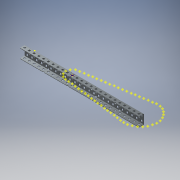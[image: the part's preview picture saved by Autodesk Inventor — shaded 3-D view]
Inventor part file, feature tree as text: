
AUTODESK INVENTOR PART (.ipt)
format: ipt  version: 2018 (Build 220112000, 112)  size: 2,780,672 bytes
history: native  units: mm (DEFAULTED — no unit token found)
features: other x277, extrude x124, sketch x4, pattern_linear x4, reference x2, imported_body x1, plane x1, mirror x1
ambient origin geometry x8: Origin, YZ Plane, XZ Plane, XY Plane, X Axis, Y Axis, Z Axis, Center Point
bodies: Solid1 (feature_tree)
feature tree (414):
  imported_body  "Base1"
  sketch  "Sketch1"  dims[d1=1.1684mm]
  pattern_linear  "Rectangular Pattern1"  Count1=25  [1 undecoded]
  pattern_linear  "Rectangular Pattern2"  Spacing1=12.7mm  [1 undecoded]
  pattern_linear  "Rectangular Pattern3"  Count1=2 Spacing1=12.7mm
  plane  "Work Plane1"
  mirror  "Mirror1"
  sketch  "Sketch3"  dims[d3=1.1684mm]
  sketch  "Sketch4"  dims[d4=0.0mm d5=250.0mm d7=12.7mm d8=20.0mm d10=12.7mm d11=240.0mm d13=12.7mm d14=1.1684mm d15=0.0mm d16=250.0mm d18=12.7mm d19=0.0mm d20=0.0mm d21=0.0mm d22=0.0mm d23=0.0mm d24=0.0mm d25=0.0mm d26=0.0mm d27=0.0mm d28=0.0mm d29=0.0mm d30=0.0mm d31=0.0mm d32=0.0mm d33=0.0mm d34=0.0mm d35=0.0mm d36=0.0mm d37=0.0mm d38=0.0mm d39=0.0mm d40=0.0mm d41=0.0mm d42=0.0mm d43=0.0mm d44=0.0mm d45=0.0mm d46=0.0mm d47=0.0mm d48=0.0mm d49=0.0mm d50=0.0mm d51=0.0mm d52=0.0mm d53=0.0mm d54=0.0mm d55=0.0mm d56=0.0mm d57=0.0mm d58=0.0mm d59=0.0mm d60=0.0mm d61=0.0mm d62=0.0mm d63=0.0mm d64=0.0mm d65=0.0mm d66=0.0mm d67=0.0mm d68=0.0mm d69=0.0mm d70=0.0mm d71=0.0mm d72=0.0mm d73=0.0mm d74=0.0mm d75=0.0mm d76=0.0mm d77=0.0mm d78=0.0mm d79=0.0mm d80=0.0mm d81=0.0mm d82=0.0mm d83=0.0mm d84=0.0mm d85=0.0mm d86=0.0mm d87=0.0mm d88=0.0mm d89=0.0mm d90=0.0mm d91=0.0mm d92=0.0mm d93=0.0mm d94=0.0mm d95=0.0mm d96=0.0mm d97=0.0mm d98=0.0mm d99=0.0mm d100=0.0mm d101=0.0mm d102=0.0mm d103=0.0mm d104=0.0mm d105=0.0mm d106=0.0mm d107=0.0mm d108=0.0mm d109=0.0mm d110=0.0mm d111=0.0mm d112=0.0mm d113=0.0mm d114=0.0mm d115=0.0mm d116=0.0mm d117=0.0mm d118=0.0mm d119=0.0mm d120=0.0mm d121=0.0mm d122=0.0mm d123=0.0mm d124=0.0mm d125=0.0mm d126=0.0mm d127=0.0mm d128=0.0mm d129=0.0mm d130=0.0mm d131=0.0mm d132=0.0mm d133=0.0mm d134=0.0mm d135=0.0mm d136=0.0mm d137=0.0mm d138=0.0mm d139=0.0mm d140=0.0mm d141=0.0mm d142=0.0mm d143=0.0mm d144=0.0mm d145=0.0mm d146=0.0mm d147=0.0mm d148=0.0mm d149=0.0mm d150=0.0mm d151=0.0mm d152=0.0mm d153=0.0mm d154=0.0mm d155=0.0mm d156=0.0mm d157=0.0mm d158=0.0mm d159=0.0mm d160=0.0mm d161=0.0mm d162=0.0mm d163=0.0mm d164=0.0mm d165=0.0mm d166=0.0mm d167=0.0mm d168=0.0mm d169=0.0mm d170=0.0mm d171=0.0mm d172=0.0mm d173=0.0mm d174=0.0mm d175=0.0mm d176=0.0mm d177=0.0mm d178=0.0mm d179=0.0mm d180=0.0mm d181=0.0mm d182=0.0mm d183=0.0mm d184=0.0mm d185=0.0mm d186=0.0mm d187=0.0mm d188=0.0mm d189=0.0mm d190=0.0mm d191=0.0mm d192=0.0mm d193=0.0mm d194=0.0mm d195=0.0mm d196=0.0mm d197=0.0mm d198=0.0mm d199=0.0mm d200=0.0mm d201=0.0mm d202=0.0mm d203=0.0mm d204=0.0mm d205=0.0mm d206=0.0mm d207=0.0mm d208=0.0mm d209=0.0mm d210=0.0mm d211=0.0mm d212=0.0mm d213=0.0mm d214=0.0mm d215=0.0mm d216=0.0mm d217=0.0mm d218=0.0mm d219=0.0mm d220=0.0mm d221=0.0mm d222=0.0mm d223=0.0mm d224=0.0mm d225=0.0mm d226=0.0mm d227=0.0mm d228=0.0mm d229=0.0mm d230=0.0mm d231=0.0mm d232=0.0mm d233=0.0mm d234=0.0mm d235=0.0mm d236=0.0mm d237=0.0mm d238=0.0mm d239=0.0mm d240=0.0mm d241=0.0mm d242=0.0mm d243=0.0mm d244=0.0mm d245=0.0mm d246=0.0mm d247=0.0mm d248=0.0mm d249=0.0mm d250=0.0mm d251=0.0mm d252=0.0mm d253=0.0mm d254=0.0mm d255=0.0mm d256=0.0mm d257=0.0mm d258=0.0mm d259=0.0mm d260=0.0mm d261=0.0mm d262=0.0mm d263=0.0mm d264=1500.0mm d266=3.715mm]
  other  "Work Point1"
  pattern_linear  "Rectangular Pattern4"  Count1=24  [1 undecoded]
  other  "Srf1"
  other  "Srf2"
  other  "Srf3"
  other  "Srf4"
  other  "Srf5"
  other  "Srf6"
  other  "Srf7"
  other  "Srf8"
  other  "Srf9"
  other  "Srf10"
  other  "Srf11"
  other  "Srf12"
  other  "Srf13"
  other  "Srf14"
  other  "Srf15"
  other  "Srf16"
  other  "Srf17"
  other  "Srf18"
  other  "Srf19"
  other  "Srf20"
  other  "Srf21"
  other  "Srf22"
  other  "Srf23"
  other  "Srf24"
  other  "Srf25"
  other  "Srf26"
  other  "Srf27"
  other  "Srf28"
  other  "Srf29"
  other  "Srf30"
  other  "Srf31"
  other  "Srf32"
  other  "Srf33"
  other  "Srf34"
  other  "Srf35"
  other  "Srf36"
  other  "Srf37"
  other  "Srf38"
  other  "Srf39"
  other  "Srf40"
  other  "Srf41"
  other  "Srf42"
  other  "Srf43"
  other  "Srf44"
  other  "Srf45"
  other  "Srf46"
  other  "Srf47"
  other  "Srf48"
  other  "Srf49"
  other  "Srf50"
  other  "Srf51"
  other  "Srf52"
  other  "Srf53"
  other  "Srf54"
  other  "Srf55"
  other  "Srf56"
  other  "Srf57"
  other  "Srf58"
  other  "Srf59"
  other  "Srf60"
  other  "Srf61"
  other  "Srf62"
  other  "Srf63"
  other  "Srf64"
  other  "Srf65"
  other  "Srf66"
  other  "Srf67"
  other  "Srf68"
  other  "Srf69"
  other  "Srf70"
  other  "Srf71"
  other  "Srf72"
  other  "Srf73"
  other  "Srf74"
  sketch  "Sketch2"  dims[d2=0.0mm]
  other  "Srf75"
  other  "Srf76"
  other  "Srf77"
  other  "Srf78"
  other  "Srf79"
  other  "Srf80"
  other  "Srf81"
  other  "Srf82"
  other  "Srf83"
  other  "Srf84"
  other  "Srf85"
  other  "Srf86"
  other  "Srf87"
  other  "Srf88"
  other  "Srf89"
  other  "Srf90"
  other  "Srf91"
  other  "Srf92"
  other  "Srf93"
  other  "Srf94"
  other  "Srf95"
  other  "Srf96"
  other  "Srf97"
  other  "Srf98"
  other  "Srf99"
  other  "Srf100"
  other  "Srf101"
  other  "Srf102"
  other  "Srf103"
  other  "Srf104"
  other  "Srf105"
  other  "Srf106"
  other  "Srf107"
  other  "Srf108"
  other  "Srf109"
  other  "Srf110"
  other  "Srf111"
  other  "Srf112"
  other  "Srf113"
  other  "Srf114"
  other  "Srf115"
  other  "Srf116"
  other  "Srf117"
  other  "Srf118"
  other  "Srf119"
  other  "Srf120"
  other  "Srf121"
  other  "Srf122"
  other  "Srf123"
  other  "Srf124"
  reference  "Reference1"
  reference  "Reference2"
  other  "Work Point2"
  other  "Work Point3"
  other  "Work Point4"
  other  "Work Point5"
  other  "Work Point6"
  other  "Work Point7"
  other  "Work Point8"
  other  "Work Point9"
  other  "Work Point10"
  other  "Work Point11"
  other  "Work Point12"
  other  "Work Point13"
  other  "Work Point14"
  other  "Work Point15"
  other  "Work Point16"
  other  "Work Point17"
  other  "Work Point18"
  other  "Work Point19"
  other  "Work Point20"
  other  "Work Point21"
  other  "Work Point22"
  other  "Work Point23"
  other  "Work Point24"
  other  "Work Point25"
  other  "Work Point26"
  other  "Work Point27"
  other  "Work Point28"
  other  "Work Point29"
  other  "Work Point30"
  other  "Work Point31"
  other  "Work Point32"
  other  "Work Point33"
  other  "Work Point34"
  other  "Work Point35"
  other  "Work Point36"
  other  "Work Point37"
  other  "Work Point38"
  other  "Work Point39"
  other  "Work Point40"
  other  "Work Point41"
  other  "Work Point42"
  other  "Work Point43"
  other  "Work Point44"
  other  "Work Point45"
  other  "Work Point46"
  other  "Work Point47"
  other  "Work Point48"
  other  "Work Point49"
  other  "Work Point50"
  other  "Work Point51"
  other  "Work Point52"
  other  "Work Point53"
  other  "Work Point54"
  other  "Work Point55"
  other  "Work Point56"
  other  "Work Point57"
  other  "Work Point58"
  other  "Work Point59"
  other  "Work Point60"
  other  "Work Point61"
  other  "Work Point62"
  other  "Work Point63"
  other  "Work Point64"
  other  "Work Point65"
  other  "Work Point66"
  other  "Work Point67"
  other  "Work Point68"
  other  "Work Point69"
  other  "Work Point70"
  other  "Work Point71"
  other  "Work Point72"
  other  "Work Point73"
  other  "Work Point74"
  other  "Work Point75"
  other  "Work Point76"
  other  "Work Point77"
  other  "Work Point78"
  other  "Work Point79"
  other  "Work Point80"
  other  "Work Point81"
  other  "Work Point82"
  other  "Work Point83"
  other  "Work Point84"
  other  "Work Point85"
  other  "Work Point86"
  other  "Work Point87"
  other  "Work Point88"
  other  "Work Point89"
  other  "Work Point90"
  other  "Work Point91"
  other  "Work Point92"
  other  "Work Point93"
  other  "Work Point94"
  other  "Work Point95"
  other  "Work Point96"
  other  "Work Point97"
  other  "Work Point98"
  other  "Work Point99"
  other  "Work Point100"
  other  "Work Point101"
  other  "Work Point102"
  other  "Work Point103"
  other  "Work Point104"
  other  "Work Point105"
  other  "Work Point106"
  other  "Work Point107"
  other  "Work Point108"
  other  "Work Point109"
  other  "Work Point110"
  other  "Work Point111"
  other  "Work Point112"
  other  "Work Point113"
  other  "Work Point114"
  other  "Work Point115"
  other  "Work Point116"
  other  "Work Point117"
  other  "Work Point118"
  other  "Work Point119"
  other  "Work Point120"
  other  "Work Point121"
  other  "Work Point122"
  other  "Work Point123"
  other  "Work Point124"
  other  "Work Point125"
  other  "Work Point126"
  other  "Work Point127"
  other  "Work Point128"
  other  "Work Point129"
  other  "Work Point130"
  other  "Work Point131"
  other  "Work Point132"
  other  "Work Point133"
  other  "Work Point134"
  other  "Work Point135"
  other  "Work Point136"
  other  "Work Point137"
  other  "Work Point138"
  other  "Work Point139"
  other  "Work Point140"
  other  "Work Point141"
  other  "Work Point142"
  other  "Work Point143"
  other  "Work Point144"
  other  "Work Point145"
  other  "Work Point146"
  other  "Work Point147"
  other  "Work Point148"
  other  "Work Point149"
  other  "Work Point150"
  extrude  "ExtrusionSrf1"  Depth=12.7mm
  extrude  "ExtrusionSrf2"  Depth=1.1684mm
  extrude  "ExtrusionSrf75"  TaperAngle=0.0deg  [1 undecoded]
  extrude  "ExtrusionSrf3"  Depth=250.0mm
  extrude  "ExtrusionSrf4"  Depth=12.7mm
  extrude  "ExtrusionSrf5"  TaperAngle=0.0deg  [1 undecoded]
  extrude  "ExtrusionSrf6"  TaperAngle=0.0deg  [1 undecoded]
  extrude  "ExtrusionSrf7"  TaperAngle=0.0deg  [1 undecoded]
  extrude  "ExtrusionSrf8"  TaperAngle=0.0deg  [1 undecoded]
  extrude  "ExtrusionSrf9"  TaperAngle=0.0deg  [1 undecoded]
  extrude  "ExtrusionSrf10"  TaperAngle=0.0deg  [1 undecoded]
  extrude  "ExtrusionSrf11"  TaperAngle=0.0deg  [1 undecoded]
  extrude  "ExtrusionSrf12"  TaperAngle=0.0deg  [1 undecoded]
  extrude  "ExtrusionSrf13"  TaperAngle=0.0deg  [1 undecoded]
  extrude  "ExtrusionSrf14"  TaperAngle=0.0deg  [1 undecoded]
  extrude  "ExtrusionSrf15"  TaperAngle=0.0deg  [1 undecoded]
  extrude  "ExtrusionSrf16"  TaperAngle=0.0deg  [1 undecoded]
  extrude  "ExtrusionSrf17"  TaperAngle=0.0deg  [1 undecoded]
  extrude  "ExtrusionSrf18"  TaperAngle=0.0deg  [1 undecoded]
  extrude  "ExtrusionSrf19"  TaperAngle=0.0deg  [1 undecoded]
  extrude  "ExtrusionSrf20"  TaperAngle=0.0deg  [1 undecoded]
  extrude  "ExtrusionSrf21"  TaperAngle=0.0deg  [1 undecoded]
  extrude  "ExtrusionSrf22"  TaperAngle=0.0deg  [1 undecoded]
  extrude  "ExtrusionSrf23"  TaperAngle=0.0deg  [1 undecoded]
  extrude  "ExtrusionSrf24"  TaperAngle=0.0deg  [1 undecoded]
  extrude  "ExtrusionSrf25"  TaperAngle=0.0deg  [1 undecoded]
  extrude  "ExtrusionSrf26"  TaperAngle=0.0deg  [1 undecoded]
  extrude  "ExtrusionSrf27"  TaperAngle=0.0deg  [1 undecoded]
  extrude  "ExtrusionSrf28"  TaperAngle=0.0deg  [1 undecoded]
  extrude  "ExtrusionSrf29"  TaperAngle=0.0deg  [1 undecoded]
  extrude  "ExtrusionSrf30"  TaperAngle=0.0deg  [1 undecoded]
  extrude  "ExtrusionSrf31"  TaperAngle=0.0deg  [1 undecoded]
  extrude  "ExtrusionSrf32"  TaperAngle=0.0deg  [1 undecoded]
  extrude  "ExtrusionSrf33"  TaperAngle=0.0deg  [1 undecoded]
  extrude  "ExtrusionSrf34"  TaperAngle=0.0deg  [1 undecoded]
  extrude  "ExtrusionSrf35"  TaperAngle=0.0deg  [1 undecoded]
  extrude  "ExtrusionSrf36"  TaperAngle=0.0deg  [1 undecoded]
  extrude  "ExtrusionSrf37"  TaperAngle=0.0deg  [1 undecoded]
  extrude  "ExtrusionSrf38"  TaperAngle=0.0deg  [1 undecoded]
  extrude  "ExtrusionSrf39"  TaperAngle=0.0deg  [1 undecoded]
  extrude  "ExtrusionSrf40"  TaperAngle=0.0deg  [1 undecoded]
  extrude  "ExtrusionSrf41"  TaperAngle=0.0deg  [1 undecoded]
  extrude  "ExtrusionSrf42"  TaperAngle=0.0deg  [1 undecoded]
  extrude  "ExtrusionSrf43"  TaperAngle=0.0deg  [1 undecoded]
  extrude  "ExtrusionSrf44"  TaperAngle=0.0deg  [1 undecoded]
  extrude  "ExtrusionSrf45"  TaperAngle=0.0deg  [1 undecoded]
  extrude  "ExtrusionSrf46"  TaperAngle=0.0deg  [1 undecoded]
  extrude  "ExtrusionSrf47"  TaperAngle=0.0deg  [1 undecoded]
  extrude  "ExtrusionSrf48"  TaperAngle=0.0deg  [1 undecoded]
  extrude  "ExtrusionSrf49"  TaperAngle=0.0deg  [1 undecoded]
  extrude  "ExtrusionSrf50"  TaperAngle=0.0deg  [1 undecoded]
  extrude  "ExtrusionSrf51"  TaperAngle=0.0deg  [1 undecoded]
  extrude  "ExtrusionSrf52"  TaperAngle=0.0deg  [1 undecoded]
  extrude  "ExtrusionSrf53"  TaperAngle=0.0deg  [1 undecoded]
  extrude  "ExtrusionSrf54"  TaperAngle=0.0deg  [1 undecoded]
  extrude  "ExtrusionSrf55"  TaperAngle=0.0deg  [1 undecoded]
  extrude  "ExtrusionSrf56"  TaperAngle=0.0deg  [1 undecoded]
  extrude  "ExtrusionSrf57"  TaperAngle=0.0deg  [1 undecoded]
  extrude  "ExtrusionSrf58"  TaperAngle=0.0deg  [1 undecoded]
  extrude  "ExtrusionSrf59"  TaperAngle=0.0deg  [1 undecoded]
  extrude  "ExtrusionSrf60"  TaperAngle=0.0deg  [1 undecoded]
  extrude  "ExtrusionSrf61"  TaperAngle=0.0deg  [1 undecoded]
  extrude  "ExtrusionSrf62"  TaperAngle=0.0deg  [1 undecoded]
  extrude  "ExtrusionSrf63"  TaperAngle=0.0deg  [1 undecoded]
  extrude  "ExtrusionSrf64"  TaperAngle=0.0deg  [1 undecoded]
  extrude  "ExtrusionSrf65"  TaperAngle=0.0deg  [1 undecoded]
  extrude  "ExtrusionSrf66"  TaperAngle=0.0deg  [1 undecoded]
  extrude  "ExtrusionSrf67"  TaperAngle=0.0deg  [1 undecoded]
  extrude  "ExtrusionSrf68"  TaperAngle=0.0deg  [1 undecoded]
  extrude  "ExtrusionSrf69"  TaperAngle=0.0deg  [1 undecoded]
  extrude  "ExtrusionSrf70"  TaperAngle=0.0deg  [1 undecoded]
  extrude  "ExtrusionSrf71"  TaperAngle=0.0deg  [1 undecoded]
  extrude  "ExtrusionSrf72"  TaperAngle=0.0deg  [1 undecoded]
  extrude  "ExtrusionSrf73"  TaperAngle=0.0deg  [1 undecoded]
  extrude  "ExtrusionSrf74"  TaperAngle=0.0deg  [1 undecoded]
  extrude  "ExtrusionSrf76"  TaperAngle=0.0deg  [1 undecoded]
  extrude  "ExtrusionSrf77"  TaperAngle=0.0deg  [1 undecoded]
  extrude  "ExtrusionSrf78"  TaperAngle=0.0deg  [1 undecoded]
  extrude  "ExtrusionSrf79"  TaperAngle=0.0deg  [1 undecoded]
  extrude  "ExtrusionSrf80"  TaperAngle=0.0deg  [1 undecoded]
  extrude  "ExtrusionSrf81"  TaperAngle=0.0deg  [1 undecoded]
  extrude  "ExtrusionSrf82"  TaperAngle=0.0deg  [1 undecoded]
  extrude  "ExtrusionSrf83"  TaperAngle=0.0deg  [1 undecoded]
  extrude  "ExtrusionSrf84"  TaperAngle=0.0deg  [1 undecoded]
  extrude  "ExtrusionSrf85"  TaperAngle=0.0deg  [1 undecoded]
  extrude  "ExtrusionSrf86"  TaperAngle=0.0deg  [1 undecoded]
  extrude  "ExtrusionSrf87"  TaperAngle=0.0deg  [1 undecoded]
  extrude  "ExtrusionSrf88"  TaperAngle=0.0deg  [1 undecoded]
  extrude  "ExtrusionSrf89"  TaperAngle=0.0deg  [1 undecoded]
  extrude  "ExtrusionSrf90"  TaperAngle=0.0deg  [1 undecoded]
  extrude  "ExtrusionSrf91"  TaperAngle=0.0deg  [1 undecoded]
  extrude  "ExtrusionSrf92"  TaperAngle=0.0deg  [1 undecoded]
  extrude  "ExtrusionSrf93"  TaperAngle=0.0deg  [1 undecoded]
  extrude  "ExtrusionSrf94"  TaperAngle=0.0deg  [1 undecoded]
  extrude  "ExtrusionSrf95"  TaperAngle=0.0deg  [1 undecoded]
  extrude  "ExtrusionSrf96"  TaperAngle=0.0deg  [1 undecoded]
  extrude  "ExtrusionSrf97"  TaperAngle=0.0deg  [1 undecoded]
  extrude  "ExtrusionSrf98"  TaperAngle=0.0deg  [1 undecoded]
  extrude  "ExtrusionSrf99"  TaperAngle=0.0deg  [1 undecoded]
  extrude  "ExtrusionSrf100"  TaperAngle=0.0deg  [1 undecoded]
  extrude  "ExtrusionSrf101"  TaperAngle=0.0deg  [1 undecoded]
  extrude  "ExtrusionSrf102"  TaperAngle=0.0deg  [1 undecoded]
  extrude  "ExtrusionSrf103"  TaperAngle=0.0deg  [1 undecoded]
  extrude  "ExtrusionSrf104"  TaperAngle=0.0deg  [1 undecoded]
  extrude  "ExtrusionSrf105"  TaperAngle=0.0deg  [1 undecoded]
  extrude  "ExtrusionSrf106"  TaperAngle=0.0deg  [1 undecoded]
  extrude  "ExtrusionSrf107"  TaperAngle=0.0deg  [1 undecoded]
  extrude  "ExtrusionSrf108"  TaperAngle=0.0deg  [1 undecoded]
  extrude  "ExtrusionSrf109"  TaperAngle=0.0deg  [1 undecoded]
  extrude  "ExtrusionSrf110"  TaperAngle=0.0deg  [1 undecoded]
  extrude  "ExtrusionSrf111"  TaperAngle=0.0deg  [1 undecoded]
  extrude  "ExtrusionSrf112"  TaperAngle=0.0deg  [1 undecoded]
  extrude  "ExtrusionSrf113"  TaperAngle=0.0deg  [1 undecoded]
  extrude  "ExtrusionSrf114"  TaperAngle=0.0deg  [1 undecoded]
  extrude  "ExtrusionSrf115"  TaperAngle=0.0deg  [1 undecoded]
  extrude  "ExtrusionSrf116"  TaperAngle=0.0deg  [1 undecoded]
  extrude  "ExtrusionSrf117"  TaperAngle=0.0deg  [1 undecoded]
  extrude  "ExtrusionSrf118"  TaperAngle=0.0deg  [1 undecoded]
  extrude  "ExtrusionSrf119"  TaperAngle=0.0deg  [1 undecoded]
  extrude  "ExtrusionSrf120"  TaperAngle=0.0deg  [1 undecoded]
  extrude  "ExtrusionSrf121"  TaperAngle=0.0deg  [1 undecoded]
  extrude  "ExtrusionSrf122"  TaperAngle=0.0deg  [1 undecoded]
  extrude  "ExtrusionSrf123"  TaperAngle=0.0deg  [1 undecoded]
  extrude  "ExtrusionSrf124"  TaperAngle=0.0deg  [1 undecoded]
  other  "Arm Manipulator.iam"
  other  "36 Tooth Gear:1"
  other  "84 Tooth Gear:4"
note: 123 required parameter values undecoded (feature->parameter linkage not recoverable at this tier; creation-order binding heuristic only, values carry confidence <= 0.55)
